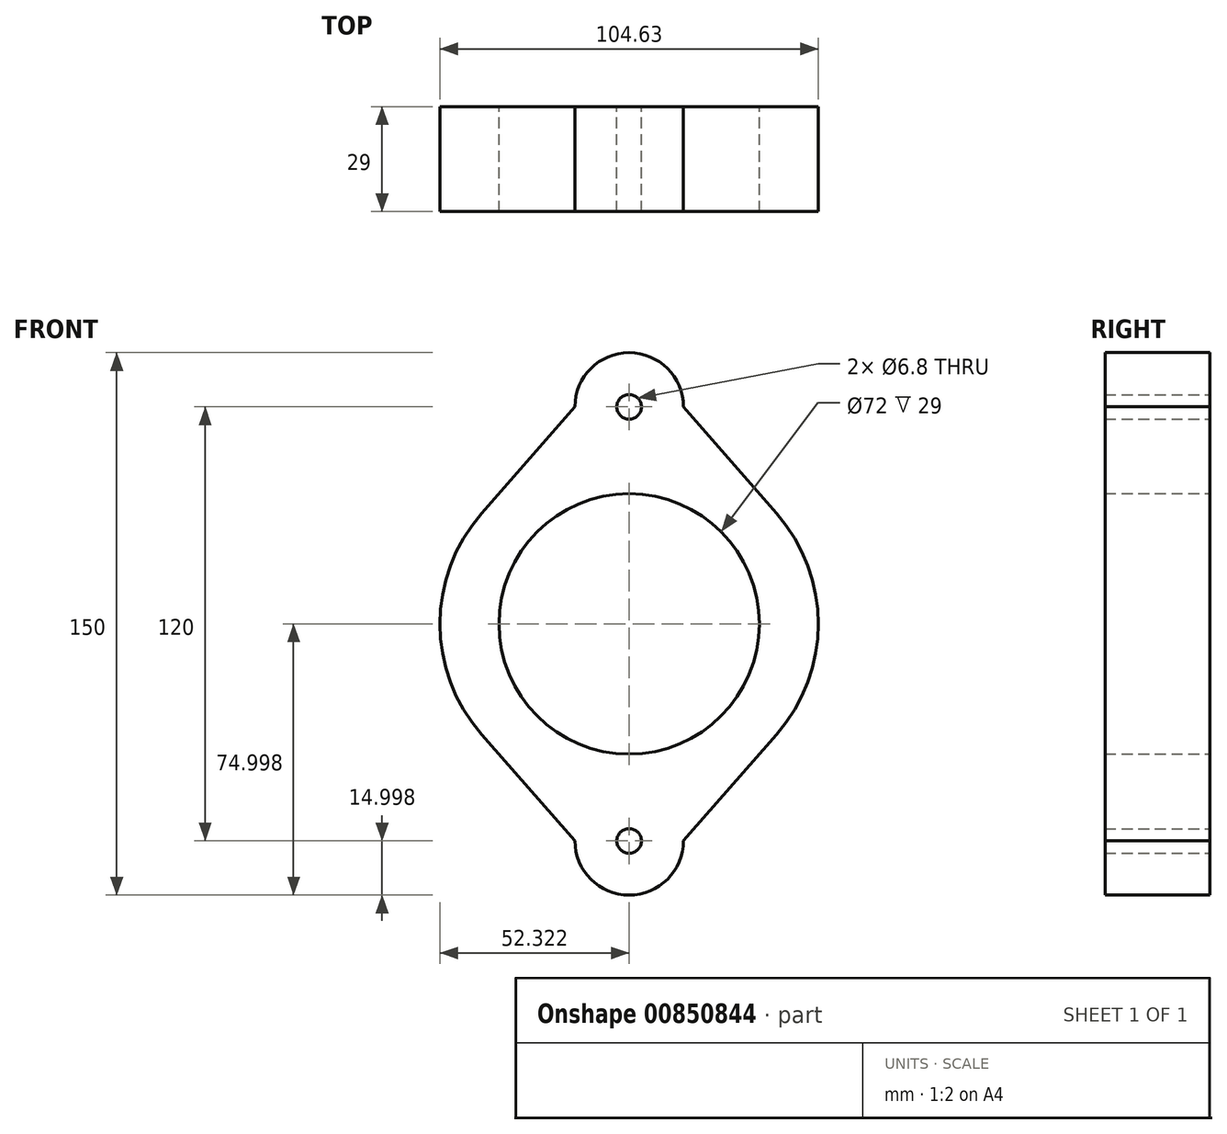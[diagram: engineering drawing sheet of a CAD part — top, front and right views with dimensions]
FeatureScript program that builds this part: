
annotation { "Feature Type Name" : "Feature", "Feature Type Description" : "" }
export const myFeature = defineFeature(function(context is Context, id is Id, definition is map)
    precondition{}
    {
        {
            var Q0;
            Q0=qCreatedBy(makeId("Front.planeOp"),FACE);
            var sketch = newSketch(context, id + "F0", { "sketchPlane" : qUnion([Q0])});
            skCircle(sketch, "E0", {"center": v(-84.8, -5.08) * mm, "radius": 36 * mm});
            skCircle(sketch, "E1", {"center": v(-84.8, 54.92) * mm, "radius": 3.4 * mm});
            skCircle(sketch, "E2", {"center": v(-84.8, -65.08) * mm, "radius": 3.4 * mm});
            skArc(sketch, "E3", {"start": v(-84.8, -80.08) * mm, "mid": v(-95.41, -75.69) * mm, "end": v(-99.8, -65.08) * mm});
            skArc(sketch, "E4", {"start": v(-84.8, -80.08) * mm, "mid": v(-74.2, -75.69) * mm, "end": v(-69.8, -65.08) * mm});
            skArc(sketch, "E5", {"start": v(-84.8, 69.92) * mm, "mid": v(-74.2, 65.52) * mm, "end": v(-69.8, 54.92) * mm});
            skArc(sketch, "E6", {"start": v(-84.8, 69.92) * mm, "mid": v(-95.41, 65.52) * mm, "end": v(-99.8, 54.92) * mm});
            skLineSegment(sketch, "E7", {"start": v(-99.8, 54.92) * mm, "end": v(-125.6, 25.52) * mm});
            skLineSegment(sketch, "E8", {"start": v(-69.8, 54.92) * mm, "end": v(-44.02, 25.52) * mm});
            skLineSegment(sketch, "E9", {"start": v(-125.6, -35.68) * mm, "end": v(-99.8, -65.08) * mm});
            skLineSegment(sketch, "E10", {"start": v(-44.02, -35.68) * mm, "end": v(-69.8, -65.08) * mm});
            skArc(sketch, "E11", {"start": v(-125.6, 25.52) * mm, "mid": v(-137.13, -5.08) * mm, "end": v(-125.6, -35.68) * mm});
            skArc(sketch, "E12", {"start": v(-44.02, -35.68) * mm, "mid": v(-32.5, -5.08) * mm, "end": v(-44.02, 25.52) * mm});
            skSolve(sketch);
        }
        {
            var Q0;
            Q0=makeQuery(id+"F0.imprint","IMPRINT",FACE,{"disambiguationData":[TD([[makeQuery(id+"F0.imprint","IMPRINT",EDGE,{"derivedFrom":sQuery(id+"F0.wireOp",EDGE,"E0")}),-1.0]])]});
            extrude(context, id + "F1", {"entities" : qUnion([Q0]), "depth" : 29 * mm, "offsetDistance" : 25.4 * mm});
        }
    });
